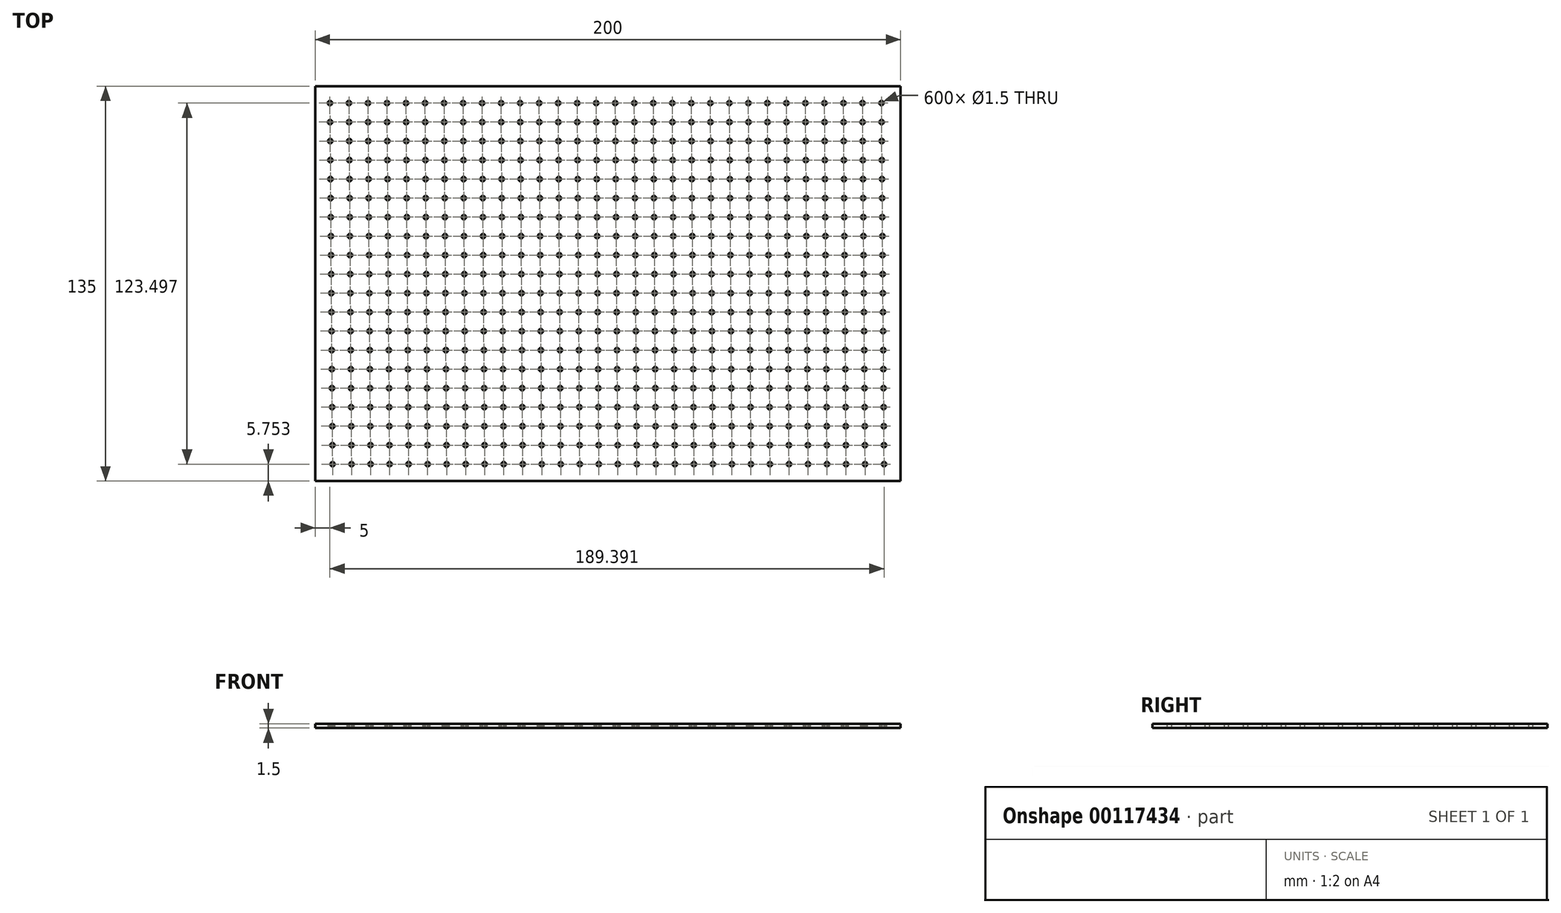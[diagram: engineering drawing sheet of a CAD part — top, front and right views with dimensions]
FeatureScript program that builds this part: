
annotation { "Feature Type Name" : "Feature", "Feature Type Description" : "" }
export const myFeature = defineFeature(function(context is Context, id is Id, definition is map)
    precondition{}
    {
        {
            var Q0;
            Q0=qCreatedBy(makeId("Top.planeOp"),FACE);
            var sketch = newSketch(context, id + "F0", { "sketchPlane" : qUnion([Q0])});
            skLineSegment(sketch, "E0.bottom", {"start": v(100, 67.5) * mm, "end": v(-100, 67.5) * mm});
            skLineSegment(sketch, "E0.top", {"start": v(100, -67.5) * mm, "end": v(-100, -67.5) * mm});
            skLineSegment(sketch, "E0.right", {"start": v(-100, 67.5) * mm, "end": v(-100, -67.5) * mm});
            skPoint(sketch, "E0.middle", {"position": v(0, 0) * mm});
            skLineSegment(sketch, "E1", {"start": v(-96.5, 67.5) * mm, "end": v(-96.5, 62.5) * mm, "construction": true});
            skLineSegment(sketch, "E2", {"start": v(-96.5, 62.5) * mm, "end": v(-100, 62.5) * mm, "construction": true});
            skLineSegment(sketch, "E3", {"start": v(-96.5, 62.5) * mm, "end": v(-95, 62.5) * mm, "construction": true});
            skLineSegment(sketch, "E4", {"start": v(-95, 62.5) * mm, "end": v(-95, 61.75) * mm, "construction": true});
            skCircle(sketch, "E5", {"center": v(-95, 61.75) * mm, "radius": 0.75 * mm});
            skCircle(sketch, "E6.1.0.0", {"center": v(-88.5, 61.75) * mm, "radius": 0.75 * mm});
            skCircle(sketch, "E6.2.0.0", {"center": v(-82, 61.75) * mm, "radius": 0.75 * mm});
            skCircle(sketch, "E6.3.0.0", {"center": v(-75.5, 61.75) * mm, "radius": 0.75 * mm});
            skCircle(sketch, "E6.4.0.0", {"center": v(-69, 61.75) * mm, "radius": 0.75 * mm});
            skCircle(sketch, "E6.5.0.0", {"center": v(-62.5, 61.75) * mm, "radius": 0.75 * mm});
            skCircle(sketch, "E6.6.0.0", {"center": v(-56, 61.75) * mm, "radius": 0.75 * mm});
            skCircle(sketch, "E6.7.0.0", {"center": v(-49.5, 61.75) * mm, "radius": 0.75 * mm});
            skCircle(sketch, "E6.8.0.0", {"center": v(-43, 61.75) * mm, "radius": 0.75 * mm});
            skCircle(sketch, "E6.9.0.0", {"center": v(-36.5, 61.75) * mm, "radius": 0.75 * mm});
            skCircle(sketch, "E6.10.0.0", {"center": v(-30, 61.75) * mm, "radius": 0.75 * mm});
            skCircle(sketch, "E6.11.0.0", {"center": v(-23.5, 61.75) * mm, "radius": 0.75 * mm});
            skCircle(sketch, "E6.12.0.0", {"center": v(-17, 61.75) * mm, "radius": 0.75 * mm});
            skCircle(sketch, "E6.13.0.0", {"center": v(-10.5, 61.75) * mm, "radius": 0.75 * mm});
            skCircle(sketch, "E6.14.0.0", {"center": v(-4, 61.75) * mm, "radius": 0.75 * mm});
            skCircle(sketch, "E6.15.0.0", {"center": v(2.5, 61.75) * mm, "radius": 0.75 * mm});
            skCircle(sketch, "E6.16.0.0", {"center": v(9, 61.75) * mm, "radius": 0.75 * mm});
            skCircle(sketch, "E6.17.0.0", {"center": v(15.5, 61.75) * mm, "radius": 0.75 * mm});
            skCircle(sketch, "E6.18.0.0", {"center": v(22, 61.75) * mm, "radius": 0.75 * mm});
            skCircle(sketch, "E6.19.0.0", {"center": v(28.5, 61.75) * mm, "radius": 0.75 * mm});
            skCircle(sketch, "E6.20.0.0", {"center": v(35, 61.75) * mm, "radius": 0.75 * mm});
            skCircle(sketch, "E6.21.0.0", {"center": v(41.5, 61.75) * mm, "radius": 0.75 * mm});
            skCircle(sketch, "E6.22.0.0", {"center": v(48, 61.75) * mm, "radius": 0.75 * mm});
            skCircle(sketch, "E6.23.0.0", {"center": v(54.5, 61.75) * mm, "radius": 0.75 * mm});
            skCircle(sketch, "E6.24.0.0", {"center": v(61, 61.75) * mm, "radius": 0.75 * mm});
            skCircle(sketch, "E6.25.0.0", {"center": v(67.5, 61.75) * mm, "radius": 0.75 * mm});
            skCircle(sketch, "E6.26.0.0", {"center": v(74, 61.75) * mm, "radius": 0.75 * mm});
            skCircle(sketch, "E6.27.0.0", {"center": v(80.5, 61.75) * mm, "radius": 0.75 * mm});
            skCircle(sketch, "E6.28.0.0", {"center": v(87, 61.75) * mm, "radius": 0.75 * mm});
            skCircle(sketch, "E6.29.0.0", {"center": v(93.5, 61.75) * mm, "radius": 0.75 * mm});
            skLineSegment(sketch, "E6.direction1", {"start": v(-95, 61.75) * mm, "end": v(-88.5, 61.75) * mm, "construction": true});
            skLineSegment(sketch, "E7", {"start": v(-95, 61.75) * mm, "end": v(-100, 61.75) * mm, "construction": true});
            skCircle(sketch, "E8.1.0.1", {"center": v(80.55, 55.25) * mm, "radius": 0.75 * mm});
            skCircle(sketch, "E8.1.0.2", {"center": v(54.55, 55.25) * mm, "radius": 0.75 * mm});
            skCircle(sketch, "E8.1.0.3", {"center": v(22.05, 55.25) * mm, "radius": 0.75 * mm});
            skCircle(sketch, "E8.1.0.7", {"center": v(28.55, 55.25) * mm, "radius": 0.75 * mm});
            skCircle(sketch, "E8.1.0.10", {"center": v(2.55, 55.25) * mm, "radius": 0.75 * mm});
            skCircle(sketch, "E8.1.0.13", {"center": v(41.55, 55.25) * mm, "radius": 0.75 * mm});
            skCircle(sketch, "E8.1.0.14", {"center": v(87.05, 55.25) * mm, "radius": 0.75 * mm});
            skCircle(sketch, "E8.1.0.16", {"center": v(61.05, 55.25) * mm, "radius": 0.75 * mm});
            skCircle(sketch, "E8.1.0.19", {"center": v(35.05, 55.25) * mm, "radius": 0.75 * mm});
            skCircle(sketch, "E8.1.0.22", {"center": v(9.05, 55.25) * mm, "radius": 0.75 * mm});
            skCircle(sketch, "E8.1.0.24", {"center": v(93.55, 55.25) * mm, "radius": 0.75 * mm});
            skCircle(sketch, "E8.1.0.25", {"center": v(48.05, 55.25) * mm, "radius": 0.75 * mm});
            skCircle(sketch, "E8.1.0.27", {"center": v(67.55, 55.25) * mm, "radius": 0.75 * mm});
            skCircle(sketch, "E8.1.0.30", {"center": v(15.55, 55.25) * mm, "radius": 0.75 * mm});
            skCircle(sketch, "E8.1.0.32", {"center": v(74.05, 55.25) * mm, "radius": 0.75 * mm});
            skCircle(sketch, "E8.1.0.35", {"center": v(-62.45, 55.25) * mm, "radius": 0.75 * mm});
            skCircle(sketch, "E8.1.0.36", {"center": v(-55.95, 55.25) * mm, "radius": 0.75 * mm});
            skCircle(sketch, "E8.1.0.37", {"center": v(-49.45, 55.25) * mm, "radius": 0.75 * mm});
            skCircle(sketch, "E8.1.0.38", {"center": v(-23.45, 55.25) * mm, "radius": 0.75 * mm});
            skCircle(sketch, "E8.1.0.39", {"center": v(-3.95, 55.25) * mm, "radius": 0.75 * mm});
            skCircle(sketch, "E8.1.0.40", {"center": v(-94.95, 55.25) * mm, "radius": 0.75 * mm});
            skCircle(sketch, "E8.1.0.41", {"center": v(-88.45, 55.25) * mm, "radius": 0.75 * mm});
            skCircle(sketch, "E8.1.0.42", {"center": v(-81.95, 55.25) * mm, "radius": 0.75 * mm});
            skCircle(sketch, "E8.1.0.43", {"center": v(-75.45, 55.25) * mm, "radius": 0.75 * mm});
            skCircle(sketch, "E8.1.0.44", {"center": v(-68.95, 55.25) * mm, "radius": 0.75 * mm});
            skCircle(sketch, "E8.1.0.45", {"center": v(-16.95, 55.25) * mm, "radius": 0.75 * mm});
            skCircle(sketch, "E8.1.0.46", {"center": v(-42.95, 55.25) * mm, "radius": 0.75 * mm});
            skCircle(sketch, "E8.1.0.47", {"center": v(-10.45, 55.25) * mm, "radius": 0.75 * mm});
            skCircle(sketch, "E8.1.0.48", {"center": v(-36.45, 55.25) * mm, "radius": 0.75 * mm});
            skCircle(sketch, "E8.1.0.49", {"center": v(-29.95, 55.25) * mm, "radius": 0.75 * mm});
            skCircle(sketch, "E8.2.0.1", {"center": v(80.6, 48.75) * mm, "radius": 0.75 * mm});
            skCircle(sketch, "E8.2.0.2", {"center": v(54.6, 48.75) * mm, "radius": 0.75 * mm});
            skCircle(sketch, "E8.2.0.3", {"center": v(22.1, 48.75) * mm, "radius": 0.75 * mm});
            skCircle(sketch, "E8.2.0.7", {"center": v(28.6, 48.75) * mm, "radius": 0.75 * mm});
            skCircle(sketch, "E8.2.0.10", {"center": v(2.6, 48.75) * mm, "radius": 0.75 * mm});
            skCircle(sketch, "E8.2.0.13", {"center": v(41.6, 48.75) * mm, "radius": 0.75 * mm});
            skCircle(sketch, "E8.2.0.14", {"center": v(87.1, 48.75) * mm, "radius": 0.75 * mm});
            skCircle(sketch, "E8.2.0.16", {"center": v(61.1, 48.75) * mm, "radius": 0.75 * mm});
            skCircle(sketch, "E8.2.0.19", {"center": v(35.1, 48.75) * mm, "radius": 0.75 * mm});
            skCircle(sketch, "E8.2.0.22", {"center": v(9.1, 48.75) * mm, "radius": 0.75 * mm});
            skCircle(sketch, "E8.2.0.24", {"center": v(93.6, 48.75) * mm, "radius": 0.75 * mm});
            skCircle(sketch, "E8.2.0.25", {"center": v(48.1, 48.75) * mm, "radius": 0.75 * mm});
            skCircle(sketch, "E8.2.0.27", {"center": v(67.6, 48.75) * mm, "radius": 0.75 * mm});
            skCircle(sketch, "E8.2.0.30", {"center": v(15.6, 48.75) * mm, "radius": 0.75 * mm});
            skCircle(sketch, "E8.2.0.32", {"center": v(74.1, 48.75) * mm, "radius": 0.75 * mm});
            skCircle(sketch, "E8.2.0.35", {"center": v(-62.4, 48.75) * mm, "radius": 0.75 * mm});
            skCircle(sketch, "E8.2.0.36", {"center": v(-55.9, 48.75) * mm, "radius": 0.75 * mm});
            skCircle(sketch, "E8.2.0.37", {"center": v(-49.4, 48.75) * mm, "radius": 0.75 * mm});
            skCircle(sketch, "E8.2.0.38", {"center": v(-23.4, 48.75) * mm, "radius": 0.75 * mm});
            skCircle(sketch, "E8.2.0.39", {"center": v(-3.9, 48.75) * mm, "radius": 0.75 * mm});
            skCircle(sketch, "E8.2.0.40", {"center": v(-94.9, 48.75) * mm, "radius": 0.75 * mm});
            skCircle(sketch, "E8.2.0.41", {"center": v(-88.4, 48.75) * mm, "radius": 0.75 * mm});
            skCircle(sketch, "E8.2.0.42", {"center": v(-81.9, 48.75) * mm, "radius": 0.75 * mm});
            skCircle(sketch, "E8.2.0.43", {"center": v(-75.4, 48.75) * mm, "radius": 0.75 * mm});
            skCircle(sketch, "E8.2.0.44", {"center": v(-68.9, 48.75) * mm, "radius": 0.75 * mm});
            skCircle(sketch, "E8.2.0.45", {"center": v(-16.9, 48.75) * mm, "radius": 0.75 * mm});
            skCircle(sketch, "E8.2.0.46", {"center": v(-42.9, 48.75) * mm, "radius": 0.75 * mm});
            skCircle(sketch, "E8.2.0.47", {"center": v(-10.4, 48.75) * mm, "radius": 0.75 * mm});
            skCircle(sketch, "E8.2.0.48", {"center": v(-36.4, 48.75) * mm, "radius": 0.75 * mm});
            skCircle(sketch, "E8.2.0.49", {"center": v(-29.9, 48.75) * mm, "radius": 0.75 * mm});
            skCircle(sketch, "E8.3.0.1", {"center": v(80.64, 42.25) * mm, "radius": 0.75 * mm});
            skCircle(sketch, "E8.3.0.2", {"center": v(54.64, 42.25) * mm, "radius": 0.75 * mm});
            skCircle(sketch, "E8.3.0.3", {"center": v(22.14, 42.25) * mm, "radius": 0.75 * mm});
            skCircle(sketch, "E8.3.0.7", {"center": v(28.64, 42.25) * mm, "radius": 0.75 * mm});
            skCircle(sketch, "E8.3.0.10", {"center": v(2.64, 42.25) * mm, "radius": 0.75 * mm});
            skCircle(sketch, "E8.3.0.13", {"center": v(41.64, 42.25) * mm, "radius": 0.75 * mm});
            skCircle(sketch, "E8.3.0.14", {"center": v(87.14, 42.25) * mm, "radius": 0.75 * mm});
            skCircle(sketch, "E8.3.0.16", {"center": v(61.14, 42.25) * mm, "radius": 0.75 * mm});
            skCircle(sketch, "E8.3.0.19", {"center": v(35.14, 42.25) * mm, "radius": 0.75 * mm});
            skCircle(sketch, "E8.3.0.22", {"center": v(9.14, 42.25) * mm, "radius": 0.75 * mm});
            skCircle(sketch, "E8.3.0.24", {"center": v(93.64, 42.25) * mm, "radius": 0.75 * mm});
            skCircle(sketch, "E8.3.0.25", {"center": v(48.14, 42.25) * mm, "radius": 0.75 * mm});
            skCircle(sketch, "E8.3.0.27", {"center": v(67.64, 42.25) * mm, "radius": 0.75 * mm});
            skCircle(sketch, "E8.3.0.30", {"center": v(15.64, 42.25) * mm, "radius": 0.75 * mm});
            skCircle(sketch, "E8.3.0.32", {"center": v(74.14, 42.25) * mm, "radius": 0.75 * mm});
            skCircle(sketch, "E8.3.0.35", {"center": v(-62.36, 42.25) * mm, "radius": 0.75 * mm});
            skCircle(sketch, "E8.3.0.36", {"center": v(-55.86, 42.25) * mm, "radius": 0.75 * mm});
            skCircle(sketch, "E8.3.0.37", {"center": v(-49.36, 42.25) * mm, "radius": 0.75 * mm});
            skCircle(sketch, "E8.3.0.38", {"center": v(-23.36, 42.25) * mm, "radius": 0.75 * mm});
            skCircle(sketch, "E8.3.0.39", {"center": v(-3.86, 42.25) * mm, "radius": 0.75 * mm});
            skCircle(sketch, "E8.3.0.40", {"center": v(-94.86, 42.25) * mm, "radius": 0.75 * mm});
            skCircle(sketch, "E8.3.0.41", {"center": v(-88.36, 42.25) * mm, "radius": 0.75 * mm});
            skCircle(sketch, "E8.3.0.42", {"center": v(-81.86, 42.25) * mm, "radius": 0.75 * mm});
            skCircle(sketch, "E8.3.0.43", {"center": v(-75.36, 42.25) * mm, "radius": 0.75 * mm});
            skCircle(sketch, "E8.3.0.44", {"center": v(-68.86, 42.25) * mm, "radius": 0.75 * mm});
            skCircle(sketch, "E8.3.0.45", {"center": v(-16.86, 42.25) * mm, "radius": 0.75 * mm});
            skCircle(sketch, "E8.3.0.46", {"center": v(-42.86, 42.25) * mm, "radius": 0.75 * mm});
            skCircle(sketch, "E8.3.0.47", {"center": v(-10.36, 42.25) * mm, "radius": 0.75 * mm});
            skCircle(sketch, "E8.3.0.48", {"center": v(-36.36, 42.25) * mm, "radius": 0.75 * mm});
            skCircle(sketch, "E8.3.0.49", {"center": v(-29.86, 42.25) * mm, "radius": 0.75 * mm});
            skCircle(sketch, "E8.4.0.1", {"center": v(80.69, 35.75) * mm, "radius": 0.75 * mm});
            skCircle(sketch, "E8.4.0.2", {"center": v(54.69, 35.75) * mm, "radius": 0.75 * mm});
            skCircle(sketch, "E8.4.0.3", {"center": v(22.19, 35.75) * mm, "radius": 0.75 * mm});
            skCircle(sketch, "E8.4.0.7", {"center": v(28.69, 35.75) * mm, "radius": 0.75 * mm});
            skCircle(sketch, "E8.4.0.10", {"center": v(2.69, 35.75) * mm, "radius": 0.75 * mm});
            skCircle(sketch, "E8.4.0.13", {"center": v(41.69, 35.75) * mm, "radius": 0.75 * mm});
            skCircle(sketch, "E8.4.0.14", {"center": v(87.19, 35.75) * mm, "radius": 0.75 * mm});
            skCircle(sketch, "E8.4.0.16", {"center": v(61.19, 35.75) * mm, "radius": 0.75 * mm});
            skCircle(sketch, "E8.4.0.19", {"center": v(35.19, 35.75) * mm, "radius": 0.75 * mm});
            skCircle(sketch, "E8.4.0.22", {"center": v(9.19, 35.75) * mm, "radius": 0.75 * mm});
            skCircle(sketch, "E8.4.0.24", {"center": v(93.69, 35.75) * mm, "radius": 0.75 * mm});
            skCircle(sketch, "E8.4.0.25", {"center": v(48.19, 35.75) * mm, "radius": 0.75 * mm});
            skCircle(sketch, "E8.4.0.27", {"center": v(67.69, 35.75) * mm, "radius": 0.75 * mm});
            skCircle(sketch, "E8.4.0.30", {"center": v(15.69, 35.75) * mm, "radius": 0.75 * mm});
            skCircle(sketch, "E8.4.0.32", {"center": v(74.19, 35.75) * mm, "radius": 0.75 * mm});
            skCircle(sketch, "E8.4.0.35", {"center": v(-62.31, 35.75) * mm, "radius": 0.75 * mm});
            skCircle(sketch, "E8.4.0.36", {"center": v(-55.81, 35.75) * mm, "radius": 0.75 * mm});
            skCircle(sketch, "E8.4.0.37", {"center": v(-49.31, 35.75) * mm, "radius": 0.75 * mm});
            skCircle(sketch, "E8.4.0.38", {"center": v(-23.31, 35.75) * mm, "radius": 0.75 * mm});
            skCircle(sketch, "E8.4.0.39", {"center": v(-3.81, 35.75) * mm, "radius": 0.75 * mm});
            skCircle(sketch, "E8.4.0.40", {"center": v(-94.81, 35.75) * mm, "radius": 0.75 * mm});
            skCircle(sketch, "E8.4.0.41", {"center": v(-88.31, 35.75) * mm, "radius": 0.75 * mm});
            skCircle(sketch, "E8.4.0.42", {"center": v(-81.81, 35.75) * mm, "radius": 0.75 * mm});
            skCircle(sketch, "E8.4.0.43", {"center": v(-75.31, 35.75) * mm, "radius": 0.75 * mm});
            skCircle(sketch, "E8.4.0.44", {"center": v(-68.81, 35.75) * mm, "radius": 0.75 * mm});
            skCircle(sketch, "E8.4.0.45", {"center": v(-16.81, 35.75) * mm, "radius": 0.75 * mm});
            skCircle(sketch, "E8.4.0.46", {"center": v(-42.81, 35.75) * mm, "radius": 0.75 * mm});
            skCircle(sketch, "E8.4.0.47", {"center": v(-10.31, 35.75) * mm, "radius": 0.75 * mm});
            skCircle(sketch, "E8.4.0.48", {"center": v(-36.31, 35.75) * mm, "radius": 0.75 * mm});
            skCircle(sketch, "E8.4.0.49", {"center": v(-29.81, 35.75) * mm, "radius": 0.75 * mm});
            skCircle(sketch, "E8.5.0.1", {"center": v(80.73, 29.25) * mm, "radius": 0.75 * mm});
            skCircle(sketch, "E8.5.0.2", {"center": v(54.73, 29.25) * mm, "radius": 0.75 * mm});
            skCircle(sketch, "E8.5.0.3", {"center": v(22.23, 29.25) * mm, "radius": 0.75 * mm});
            skCircle(sketch, "E8.5.0.7", {"center": v(28.73, 29.25) * mm, "radius": 0.75 * mm});
            skCircle(sketch, "E8.5.0.10", {"center": v(2.73, 29.25) * mm, "radius": 0.75 * mm});
            skCircle(sketch, "E8.5.0.13", {"center": v(41.73, 29.25) * mm, "radius": 0.75 * mm});
            skCircle(sketch, "E8.5.0.14", {"center": v(87.23, 29.25) * mm, "radius": 0.75 * mm});
            skCircle(sketch, "E8.5.0.16", {"center": v(61.23, 29.25) * mm, "radius": 0.75 * mm});
            skCircle(sketch, "E8.5.0.19", {"center": v(35.23, 29.25) * mm, "radius": 0.75 * mm});
            skCircle(sketch, "E8.5.0.22", {"center": v(9.23, 29.25) * mm, "radius": 0.75 * mm});
            skCircle(sketch, "E8.5.0.24", {"center": v(93.73, 29.25) * mm, "radius": 0.75 * mm});
            skCircle(sketch, "E8.5.0.25", {"center": v(48.23, 29.25) * mm, "radius": 0.75 * mm});
            skCircle(sketch, "E8.5.0.27", {"center": v(67.73, 29.25) * mm, "radius": 0.75 * mm});
            skCircle(sketch, "E8.5.0.30", {"center": v(15.73, 29.25) * mm, "radius": 0.75 * mm});
            skCircle(sketch, "E8.5.0.32", {"center": v(74.23, 29.25) * mm, "radius": 0.75 * mm});
            skCircle(sketch, "E8.5.0.35", {"center": v(-62.27, 29.25) * mm, "radius": 0.75 * mm});
            skCircle(sketch, "E8.5.0.36", {"center": v(-55.77, 29.25) * mm, "radius": 0.75 * mm});
            skCircle(sketch, "E8.5.0.37", {"center": v(-49.27, 29.25) * mm, "radius": 0.75 * mm});
            skCircle(sketch, "E8.5.0.38", {"center": v(-23.27, 29.25) * mm, "radius": 0.75 * mm});
            skCircle(sketch, "E8.5.0.39", {"center": v(-3.77, 29.25) * mm, "radius": 0.75 * mm});
            skCircle(sketch, "E8.5.0.40", {"center": v(-94.77, 29.25) * mm, "radius": 0.75 * mm});
            skCircle(sketch, "E8.5.0.41", {"center": v(-88.27, 29.25) * mm, "radius": 0.75 * mm});
            skCircle(sketch, "E8.5.0.42", {"center": v(-81.77, 29.25) * mm, "radius": 0.75 * mm});
            skCircle(sketch, "E8.5.0.43", {"center": v(-75.27, 29.25) * mm, "radius": 0.75 * mm});
            skCircle(sketch, "E8.5.0.44", {"center": v(-68.77, 29.25) * mm, "radius": 0.75 * mm});
            skCircle(sketch, "E8.5.0.45", {"center": v(-16.77, 29.25) * mm, "radius": 0.75 * mm});
            skCircle(sketch, "E8.5.0.46", {"center": v(-42.77, 29.25) * mm, "radius": 0.75 * mm});
            skCircle(sketch, "E8.5.0.47", {"center": v(-10.27, 29.25) * mm, "radius": 0.75 * mm});
            skCircle(sketch, "E8.5.0.48", {"center": v(-36.27, 29.25) * mm, "radius": 0.75 * mm});
            skCircle(sketch, "E8.5.0.49", {"center": v(-29.77, 29.25) * mm, "radius": 0.75 * mm});
            skCircle(sketch, "E8.6.0.1", {"center": v(80.78, 22.75) * mm, "radius": 0.75 * mm});
            skCircle(sketch, "E8.6.0.2", {"center": v(54.78, 22.75) * mm, "radius": 0.75 * mm});
            skCircle(sketch, "E8.6.0.3", {"center": v(22.28, 22.75) * mm, "radius": 0.75 * mm});
            skCircle(sketch, "E8.6.0.7", {"center": v(28.78, 22.75) * mm, "radius": 0.75 * mm});
            skCircle(sketch, "E8.6.0.10", {"center": v(2.78, 22.75) * mm, "radius": 0.75 * mm});
            skCircle(sketch, "E8.6.0.13", {"center": v(41.78, 22.75) * mm, "radius": 0.75 * mm});
            skCircle(sketch, "E8.6.0.14", {"center": v(87.28, 22.75) * mm, "radius": 0.75 * mm});
            skCircle(sketch, "E8.6.0.16", {"center": v(61.28, 22.75) * mm, "radius": 0.75 * mm});
            skCircle(sketch, "E8.6.0.19", {"center": v(35.28, 22.75) * mm, "radius": 0.75 * mm});
            skCircle(sketch, "E8.6.0.22", {"center": v(9.28, 22.75) * mm, "radius": 0.75 * mm});
            skCircle(sketch, "E8.6.0.24", {"center": v(93.78, 22.75) * mm, "radius": 0.75 * mm});
            skCircle(sketch, "E8.6.0.25", {"center": v(48.28, 22.75) * mm, "radius": 0.75 * mm});
            skCircle(sketch, "E8.6.0.27", {"center": v(67.78, 22.75) * mm, "radius": 0.75 * mm});
            skCircle(sketch, "E8.6.0.30", {"center": v(15.78, 22.75) * mm, "radius": 0.75 * mm});
            skCircle(sketch, "E8.6.0.32", {"center": v(74.28, 22.75) * mm, "radius": 0.75 * mm});
            skCircle(sketch, "E8.6.0.35", {"center": v(-62.22, 22.75) * mm, "radius": 0.75 * mm});
            skCircle(sketch, "E8.6.0.36", {"center": v(-55.72, 22.75) * mm, "radius": 0.75 * mm});
            skCircle(sketch, "E8.6.0.37", {"center": v(-49.22, 22.75) * mm, "radius": 0.75 * mm});
            skCircle(sketch, "E8.6.0.38", {"center": v(-23.22, 22.75) * mm, "radius": 0.75 * mm});
            skCircle(sketch, "E8.6.0.39", {"center": v(-3.72, 22.75) * mm, "radius": 0.75 * mm});
            skCircle(sketch, "E8.6.0.40", {"center": v(-94.72, 22.75) * mm, "radius": 0.75 * mm});
            skCircle(sketch, "E8.6.0.41", {"center": v(-88.22, 22.75) * mm, "radius": 0.75 * mm});
            skCircle(sketch, "E8.6.0.42", {"center": v(-81.72, 22.75) * mm, "radius": 0.75 * mm});
            skCircle(sketch, "E8.6.0.43", {"center": v(-75.22, 22.75) * mm, "radius": 0.75 * mm});
            skCircle(sketch, "E8.6.0.44", {"center": v(-68.72, 22.75) * mm, "radius": 0.75 * mm});
            skCircle(sketch, "E8.6.0.45", {"center": v(-16.72, 22.75) * mm, "radius": 0.75 * mm});
            skCircle(sketch, "E8.6.0.46", {"center": v(-42.72, 22.75) * mm, "radius": 0.75 * mm});
            skCircle(sketch, "E8.6.0.47", {"center": v(-10.22, 22.75) * mm, "radius": 0.75 * mm});
            skCircle(sketch, "E8.6.0.48", {"center": v(-36.22, 22.75) * mm, "radius": 0.75 * mm});
            skCircle(sketch, "E8.6.0.49", {"center": v(-29.72, 22.75) * mm, "radius": 0.75 * mm});
            skCircle(sketch, "E8.7.0.1", {"center": v(80.83, 16.25) * mm, "radius": 0.75 * mm});
            skCircle(sketch, "E8.7.0.2", {"center": v(54.83, 16.25) * mm, "radius": 0.75 * mm});
            skCircle(sketch, "E8.7.0.3", {"center": v(22.33, 16.25) * mm, "radius": 0.75 * mm});
            skCircle(sketch, "E8.7.0.7", {"center": v(28.83, 16.25) * mm, "radius": 0.75 * mm});
            skCircle(sketch, "E8.7.0.10", {"center": v(2.83, 16.25) * mm, "radius": 0.75 * mm});
            skCircle(sketch, "E8.7.0.13", {"center": v(41.83, 16.25) * mm, "radius": 0.75 * mm});
            skCircle(sketch, "E8.7.0.14", {"center": v(87.33, 16.25) * mm, "radius": 0.75 * mm});
            skCircle(sketch, "E8.7.0.16", {"center": v(61.33, 16.25) * mm, "radius": 0.75 * mm});
            skCircle(sketch, "E8.7.0.19", {"center": v(35.33, 16.25) * mm, "radius": 0.75 * mm});
            skCircle(sketch, "E8.7.0.22", {"center": v(9.33, 16.25) * mm, "radius": 0.75 * mm});
            skCircle(sketch, "E8.7.0.24", {"center": v(93.83, 16.25) * mm, "radius": 0.75 * mm});
            skCircle(sketch, "E8.7.0.25", {"center": v(48.33, 16.25) * mm, "radius": 0.75 * mm});
            skCircle(sketch, "E8.7.0.27", {"center": v(67.83, 16.25) * mm, "radius": 0.75 * mm});
            skCircle(sketch, "E8.7.0.30", {"center": v(15.83, 16.25) * mm, "radius": 0.75 * mm});
            skCircle(sketch, "E8.7.0.32", {"center": v(74.33, 16.25) * mm, "radius": 0.75 * mm});
            skCircle(sketch, "E8.7.0.35", {"center": v(-62.17, 16.25) * mm, "radius": 0.75 * mm});
            skCircle(sketch, "E8.7.0.36", {"center": v(-55.67, 16.25) * mm, "radius": 0.75 * mm});
            skCircle(sketch, "E8.7.0.37", {"center": v(-49.17, 16.25) * mm, "radius": 0.75 * mm});
            skCircle(sketch, "E8.7.0.38", {"center": v(-23.17, 16.25) * mm, "radius": 0.75 * mm});
            skCircle(sketch, "E8.7.0.39", {"center": v(-3.67, 16.25) * mm, "radius": 0.75 * mm});
            skCircle(sketch, "E8.7.0.40", {"center": v(-94.67, 16.25) * mm, "radius": 0.75 * mm});
            skCircle(sketch, "E8.7.0.41", {"center": v(-88.17, 16.25) * mm, "radius": 0.75 * mm});
            skCircle(sketch, "E8.7.0.42", {"center": v(-81.67, 16.25) * mm, "radius": 0.75 * mm});
            skCircle(sketch, "E8.7.0.43", {"center": v(-75.17, 16.25) * mm, "radius": 0.75 * mm});
            skCircle(sketch, "E8.7.0.44", {"center": v(-68.67, 16.25) * mm, "radius": 0.75 * mm});
            skCircle(sketch, "E8.7.0.45", {"center": v(-16.67, 16.25) * mm, "radius": 0.75 * mm});
            skCircle(sketch, "E8.7.0.46", {"center": v(-42.67, 16.25) * mm, "radius": 0.75 * mm});
            skCircle(sketch, "E8.7.0.47", {"center": v(-10.17, 16.25) * mm, "radius": 0.75 * mm});
            skCircle(sketch, "E8.7.0.48", {"center": v(-36.17, 16.25) * mm, "radius": 0.75 * mm});
            skCircle(sketch, "E8.7.0.49", {"center": v(-29.67, 16.25) * mm, "radius": 0.75 * mm});
            skCircle(sketch, "E8.8.0.1", {"center": v(80.88, 9.75) * mm, "radius": 0.75 * mm});
            skCircle(sketch, "E8.8.0.2", {"center": v(54.88, 9.75) * mm, "radius": 0.75 * mm});
            skCircle(sketch, "E8.8.0.3", {"center": v(22.38, 9.75) * mm, "radius": 0.75 * mm});
            skCircle(sketch, "E8.8.0.7", {"center": v(28.88, 9.75) * mm, "radius": 0.75 * mm});
            skCircle(sketch, "E8.8.0.10", {"center": v(2.88, 9.75) * mm, "radius": 0.75 * mm});
            skCircle(sketch, "E8.8.0.13", {"center": v(41.88, 9.75) * mm, "radius": 0.75 * mm});
            skCircle(sketch, "E8.8.0.14", {"center": v(87.38, 9.75) * mm, "radius": 0.75 * mm});
            skCircle(sketch, "E8.8.0.16", {"center": v(61.38, 9.75) * mm, "radius": 0.75 * mm});
            skCircle(sketch, "E8.8.0.19", {"center": v(35.38, 9.75) * mm, "radius": 0.75 * mm});
            skCircle(sketch, "E8.8.0.22", {"center": v(9.38, 9.75) * mm, "radius": 0.75 * mm});
            skCircle(sketch, "E8.8.0.24", {"center": v(93.88, 9.75) * mm, "radius": 0.75 * mm});
            skCircle(sketch, "E8.8.0.25", {"center": v(48.38, 9.75) * mm, "radius": 0.75 * mm});
            skCircle(sketch, "E8.8.0.27", {"center": v(67.88, 9.75) * mm, "radius": 0.75 * mm});
            skCircle(sketch, "E8.8.0.30", {"center": v(15.88, 9.75) * mm, "radius": 0.75 * mm});
            skCircle(sketch, "E8.8.0.32", {"center": v(74.38, 9.75) * mm, "radius": 0.75 * mm});
            skCircle(sketch, "E8.8.0.35", {"center": v(-62.12, 9.75) * mm, "radius": 0.75 * mm});
            skCircle(sketch, "E8.8.0.36", {"center": v(-55.62, 9.75) * mm, "radius": 0.75 * mm});
            skCircle(sketch, "E8.8.0.37", {"center": v(-49.12, 9.75) * mm, "radius": 0.75 * mm});
            skCircle(sketch, "E8.8.0.38", {"center": v(-23.12, 9.75) * mm, "radius": 0.75 * mm});
            skCircle(sketch, "E8.8.0.39", {"center": v(-3.62, 9.75) * mm, "radius": 0.75 * mm});
            skCircle(sketch, "E8.8.0.40", {"center": v(-94.62, 9.75) * mm, "radius": 0.75 * mm});
            skCircle(sketch, "E8.8.0.41", {"center": v(-88.12, 9.75) * mm, "radius": 0.75 * mm});
            skCircle(sketch, "E8.8.0.42", {"center": v(-81.62, 9.75) * mm, "radius": 0.75 * mm});
            skCircle(sketch, "E8.8.0.43", {"center": v(-75.12, 9.75) * mm, "radius": 0.75 * mm});
            skCircle(sketch, "E8.8.0.44", {"center": v(-68.62, 9.75) * mm, "radius": 0.75 * mm});
            skCircle(sketch, "E8.8.0.45", {"center": v(-16.62, 9.75) * mm, "radius": 0.75 * mm});
            skCircle(sketch, "E8.8.0.46", {"center": v(-42.62, 9.75) * mm, "radius": 0.75 * mm});
            skCircle(sketch, "E8.8.0.47", {"center": v(-10.12, 9.75) * mm, "radius": 0.75 * mm});
            skCircle(sketch, "E8.8.0.48", {"center": v(-36.12, 9.75) * mm, "radius": 0.75 * mm});
            skCircle(sketch, "E8.8.0.49", {"center": v(-29.62, 9.75) * mm, "radius": 0.75 * mm});
            skCircle(sketch, "E8.9.0.1", {"center": v(80.92, 3.25) * mm, "radius": 0.75 * mm});
            skCircle(sketch, "E8.9.0.2", {"center": v(54.92, 3.25) * mm, "radius": 0.75 * mm});
            skCircle(sketch, "E8.9.0.3", {"center": v(22.42, 3.25) * mm, "radius": 0.75 * mm});
            skCircle(sketch, "E8.9.0.7", {"center": v(28.92, 3.25) * mm, "radius": 0.75 * mm});
            skCircle(sketch, "E8.9.0.10", {"center": v(2.92, 3.25) * mm, "radius": 0.75 * mm});
            skCircle(sketch, "E8.9.0.13", {"center": v(41.92, 3.25) * mm, "radius": 0.75 * mm});
            skCircle(sketch, "E8.9.0.14", {"center": v(87.42, 3.25) * mm, "radius": 0.75 * mm});
            skCircle(sketch, "E8.9.0.16", {"center": v(61.42, 3.25) * mm, "radius": 0.75 * mm});
            skCircle(sketch, "E8.9.0.19", {"center": v(35.42, 3.25) * mm, "radius": 0.75 * mm});
            skCircle(sketch, "E8.9.0.22", {"center": v(9.42, 3.25) * mm, "radius": 0.75 * mm});
            skCircle(sketch, "E8.9.0.24", {"center": v(93.92, 3.25) * mm, "radius": 0.75 * mm});
            skCircle(sketch, "E8.9.0.25", {"center": v(48.42, 3.25) * mm, "radius": 0.75 * mm});
            skCircle(sketch, "E8.9.0.27", {"center": v(67.92, 3.25) * mm, "radius": 0.75 * mm});
            skCircle(sketch, "E8.9.0.30", {"center": v(15.92, 3.25) * mm, "radius": 0.75 * mm});
            skCircle(sketch, "E8.9.0.32", {"center": v(74.42, 3.25) * mm, "radius": 0.75 * mm});
            skCircle(sketch, "E8.9.0.35", {"center": v(-62.08, 3.25) * mm, "radius": 0.75 * mm});
            skCircle(sketch, "E8.9.0.36", {"center": v(-55.58, 3.25) * mm, "radius": 0.75 * mm});
            skCircle(sketch, "E8.9.0.37", {"center": v(-49.08, 3.25) * mm, "radius": 0.75 * mm});
            skCircle(sketch, "E8.9.0.38", {"center": v(-23.08, 3.25) * mm, "radius": 0.75 * mm});
            skCircle(sketch, "E8.9.0.39", {"center": v(-3.58, 3.25) * mm, "radius": 0.75 * mm});
            skCircle(sketch, "E8.9.0.40", {"center": v(-94.58, 3.25) * mm, "radius": 0.75 * mm});
            skCircle(sketch, "E8.9.0.41", {"center": v(-88.08, 3.25) * mm, "radius": 0.75 * mm});
            skCircle(sketch, "E8.9.0.42", {"center": v(-81.58, 3.25) * mm, "radius": 0.75 * mm});
            skCircle(sketch, "E8.9.0.43", {"center": v(-75.08, 3.25) * mm, "radius": 0.75 * mm});
            skCircle(sketch, "E8.9.0.44", {"center": v(-68.58, 3.25) * mm, "radius": 0.75 * mm});
            skCircle(sketch, "E8.9.0.45", {"center": v(-16.58, 3.25) * mm, "radius": 0.75 * mm});
            skCircle(sketch, "E8.9.0.46", {"center": v(-42.58, 3.25) * mm, "radius": 0.75 * mm});
            skCircle(sketch, "E8.9.0.47", {"center": v(-10.08, 3.25) * mm, "radius": 0.75 * mm});
            skCircle(sketch, "E8.9.0.48", {"center": v(-36.08, 3.25) * mm, "radius": 0.75 * mm});
            skCircle(sketch, "E8.9.0.49", {"center": v(-29.58, 3.25) * mm, "radius": 0.75 * mm});
            skCircle(sketch, "E8.10.0.1", {"center": v(80.97, -3.25) * mm, "radius": 0.75 * mm});
            skCircle(sketch, "E8.10.0.2", {"center": v(54.97, -3.25) * mm, "radius": 0.75 * mm});
            skCircle(sketch, "E8.10.0.3", {"center": v(22.47, -3.25) * mm, "radius": 0.75 * mm});
            skCircle(sketch, "E8.10.0.7", {"center": v(28.97, -3.25) * mm, "radius": 0.75 * mm});
            skCircle(sketch, "E8.10.0.10", {"center": v(2.97, -3.25) * mm, "radius": 0.75 * mm});
            skCircle(sketch, "E8.10.0.13", {"center": v(41.97, -3.25) * mm, "radius": 0.75 * mm});
            skCircle(sketch, "E8.10.0.14", {"center": v(87.47, -3.25) * mm, "radius": 0.75 * mm});
            skCircle(sketch, "E8.10.0.16", {"center": v(61.47, -3.25) * mm, "radius": 0.75 * mm});
            skCircle(sketch, "E8.10.0.19", {"center": v(35.47, -3.25) * mm, "radius": 0.75 * mm});
            skCircle(sketch, "E8.10.0.22", {"center": v(9.47, -3.25) * mm, "radius": 0.75 * mm});
            skCircle(sketch, "E8.10.0.24", {"center": v(93.97, -3.25) * mm, "radius": 0.75 * mm});
            skCircle(sketch, "E8.10.0.25", {"center": v(48.47, -3.25) * mm, "radius": 0.75 * mm});
            skCircle(sketch, "E8.10.0.27", {"center": v(67.97, -3.25) * mm, "radius": 0.75 * mm});
            skCircle(sketch, "E8.10.0.30", {"center": v(15.97, -3.25) * mm, "radius": 0.75 * mm});
            skCircle(sketch, "E8.10.0.32", {"center": v(74.47, -3.25) * mm, "radius": 0.75 * mm});
            skCircle(sketch, "E8.10.0.35", {"center": v(-62.03, -3.25) * mm, "radius": 0.75 * mm});
            skCircle(sketch, "E8.10.0.36", {"center": v(-55.53, -3.25) * mm, "radius": 0.75 * mm});
            skCircle(sketch, "E8.10.0.37", {"center": v(-49.03, -3.25) * mm, "radius": 0.75 * mm});
            skCircle(sketch, "E8.10.0.38", {"center": v(-23.03, -3.25) * mm, "radius": 0.75 * mm});
            skCircle(sketch, "E8.10.0.39", {"center": v(-3.53, -3.25) * mm, "radius": 0.75 * mm});
            skCircle(sketch, "E8.10.0.40", {"center": v(-94.53, -3.25) * mm, "radius": 0.75 * mm});
            skCircle(sketch, "E8.10.0.41", {"center": v(-88.03, -3.25) * mm, "radius": 0.75 * mm});
            skCircle(sketch, "E8.10.0.42", {"center": v(-81.53, -3.25) * mm, "radius": 0.75 * mm});
            skCircle(sketch, "E8.10.0.43", {"center": v(-75.03, -3.25) * mm, "radius": 0.75 * mm});
            skCircle(sketch, "E8.10.0.44", {"center": v(-68.53, -3.25) * mm, "radius": 0.75 * mm});
            skCircle(sketch, "E8.10.0.45", {"center": v(-16.53, -3.25) * mm, "radius": 0.75 * mm});
            skCircle(sketch, "E8.10.0.46", {"center": v(-42.53, -3.25) * mm, "radius": 0.75 * mm});
            skCircle(sketch, "E8.10.0.47", {"center": v(-10.03, -3.25) * mm, "radius": 0.75 * mm});
            skCircle(sketch, "E8.10.0.48", {"center": v(-36.03, -3.25) * mm, "radius": 0.75 * mm});
            skCircle(sketch, "E8.10.0.49", {"center": v(-29.53, -3.25) * mm, "radius": 0.75 * mm});
            skCircle(sketch, "E8.11.0.1", {"center": v(81.02, -9.75) * mm, "radius": 0.75 * mm});
            skCircle(sketch, "E8.11.0.2", {"center": v(55.02, -9.75) * mm, "radius": 0.75 * mm});
            skCircle(sketch, "E8.11.0.3", {"center": v(22.52, -9.75) * mm, "radius": 0.75 * mm});
            skCircle(sketch, "E8.11.0.7", {"center": v(29.02, -9.75) * mm, "radius": 0.75 * mm});
            skCircle(sketch, "E8.11.0.10", {"center": v(3.02, -9.75) * mm, "radius": 0.75 * mm});
            skCircle(sketch, "E8.11.0.13", {"center": v(42.02, -9.75) * mm, "radius": 0.75 * mm});
            skCircle(sketch, "E8.11.0.14", {"center": v(87.52, -9.75) * mm, "radius": 0.75 * mm});
            skCircle(sketch, "E8.11.0.16", {"center": v(61.52, -9.75) * mm, "radius": 0.75 * mm});
            skCircle(sketch, "E8.11.0.19", {"center": v(35.52, -9.75) * mm, "radius": 0.75 * mm});
            skCircle(sketch, "E8.11.0.22", {"center": v(9.52, -9.75) * mm, "radius": 0.75 * mm});
            skCircle(sketch, "E8.11.0.24", {"center": v(94.02, -9.75) * mm, "radius": 0.75 * mm});
            skCircle(sketch, "E8.11.0.25", {"center": v(48.52, -9.75) * mm, "radius": 0.75 * mm});
            skCircle(sketch, "E8.11.0.27", {"center": v(68.02, -9.75) * mm, "radius": 0.75 * mm});
            skCircle(sketch, "E8.11.0.30", {"center": v(16.02, -9.75) * mm, "radius": 0.75 * mm});
            skCircle(sketch, "E8.11.0.32", {"center": v(74.52, -9.75) * mm, "radius": 0.75 * mm});
            skCircle(sketch, "E8.11.0.35", {"center": v(-61.98, -9.75) * mm, "radius": 0.75 * mm});
            skCircle(sketch, "E8.11.0.36", {"center": v(-55.48, -9.75) * mm, "radius": 0.75 * mm});
            skCircle(sketch, "E8.11.0.37", {"center": v(-48.98, -9.75) * mm, "radius": 0.75 * mm});
            skCircle(sketch, "E8.11.0.38", {"center": v(-22.98, -9.75) * mm, "radius": 0.75 * mm});
            skCircle(sketch, "E8.11.0.39", {"center": v(-3.48, -9.75) * mm, "radius": 0.75 * mm});
            skCircle(sketch, "E8.11.0.40", {"center": v(-94.48, -9.75) * mm, "radius": 0.75 * mm});
            skCircle(sketch, "E8.11.0.41", {"center": v(-87.98, -9.75) * mm, "radius": 0.75 * mm});
            skCircle(sketch, "E8.11.0.42", {"center": v(-81.48, -9.75) * mm, "radius": 0.75 * mm});
            skCircle(sketch, "E8.11.0.43", {"center": v(-74.98, -9.75) * mm, "radius": 0.75 * mm});
            skCircle(sketch, "E8.11.0.44", {"center": v(-68.48, -9.75) * mm, "radius": 0.75 * mm});
            skCircle(sketch, "E8.11.0.45", {"center": v(-16.48, -9.75) * mm, "radius": 0.75 * mm});
            skCircle(sketch, "E8.11.0.46", {"center": v(-42.48, -9.75) * mm, "radius": 0.75 * mm});
            skCircle(sketch, "E8.11.0.47", {"center": v(-9.98, -9.75) * mm, "radius": 0.75 * mm});
            skCircle(sketch, "E8.11.0.48", {"center": v(-35.98, -9.75) * mm, "radius": 0.75 * mm});
            skCircle(sketch, "E8.11.0.49", {"center": v(-29.48, -9.75) * mm, "radius": 0.75 * mm});
            skCircle(sketch, "E8.12.0.1", {"center": v(81.06, -16.25) * mm, "radius": 0.75 * mm});
            skCircle(sketch, "E8.12.0.2", {"center": v(55.06, -16.25) * mm, "radius": 0.75 * mm});
            skCircle(sketch, "E8.12.0.3", {"center": v(22.56, -16.25) * mm, "radius": 0.75 * mm});
            skCircle(sketch, "E8.12.0.7", {"center": v(29.06, -16.25) * mm, "radius": 0.75 * mm});
            skCircle(sketch, "E8.12.0.10", {"center": v(3.06, -16.25) * mm, "radius": 0.75 * mm});
            skCircle(sketch, "E8.12.0.13", {"center": v(42.06, -16.25) * mm, "radius": 0.75 * mm});
            skCircle(sketch, "E8.12.0.14", {"center": v(87.56, -16.25) * mm, "radius": 0.75 * mm});
            skCircle(sketch, "E8.12.0.16", {"center": v(61.56, -16.25) * mm, "radius": 0.75 * mm});
            skCircle(sketch, "E8.12.0.19", {"center": v(35.56, -16.25) * mm, "radius": 0.75 * mm});
            skCircle(sketch, "E8.12.0.22", {"center": v(9.56, -16.25) * mm, "radius": 0.75 * mm});
            skCircle(sketch, "E8.12.0.24", {"center": v(94.06, -16.25) * mm, "radius": 0.75 * mm});
            skCircle(sketch, "E8.12.0.25", {"center": v(48.56, -16.25) * mm, "radius": 0.75 * mm});
            skCircle(sketch, "E8.12.0.27", {"center": v(68.06, -16.25) * mm, "radius": 0.75 * mm});
            skCircle(sketch, "E8.12.0.30", {"center": v(16.06, -16.25) * mm, "radius": 0.75 * mm});
            skCircle(sketch, "E8.12.0.32", {"center": v(74.56, -16.25) * mm, "radius": 0.75 * mm});
            skCircle(sketch, "E8.12.0.35", {"center": v(-61.94, -16.25) * mm, "radius": 0.75 * mm});
            skCircle(sketch, "E8.12.0.36", {"center": v(-55.44, -16.25) * mm, "radius": 0.75 * mm});
            skCircle(sketch, "E8.12.0.37", {"center": v(-48.94, -16.25) * mm, "radius": 0.75 * mm});
            skCircle(sketch, "E8.12.0.38", {"center": v(-22.94, -16.25) * mm, "radius": 0.75 * mm});
            skCircle(sketch, "E8.12.0.39", {"center": v(-3.44, -16.25) * mm, "radius": 0.75 * mm});
            skCircle(sketch, "E8.12.0.40", {"center": v(-94.44, -16.25) * mm, "radius": 0.75 * mm});
            skCircle(sketch, "E8.12.0.41", {"center": v(-87.94, -16.25) * mm, "radius": 0.75 * mm});
            skCircle(sketch, "E8.12.0.42", {"center": v(-81.44, -16.25) * mm, "radius": 0.75 * mm});
            skCircle(sketch, "E8.12.0.43", {"center": v(-74.94, -16.25) * mm, "radius": 0.75 * mm});
            skCircle(sketch, "E8.12.0.44", {"center": v(-68.44, -16.25) * mm, "radius": 0.75 * mm});
            skCircle(sketch, "E8.12.0.45", {"center": v(-16.44, -16.25) * mm, "radius": 0.75 * mm});
            skCircle(sketch, "E8.12.0.46", {"center": v(-42.44, -16.25) * mm, "radius": 0.75 * mm});
            skCircle(sketch, "E8.12.0.47", {"center": v(-9.94, -16.25) * mm, "radius": 0.75 * mm});
            skCircle(sketch, "E8.12.0.48", {"center": v(-35.94, -16.25) * mm, "radius": 0.75 * mm});
            skCircle(sketch, "E8.12.0.49", {"center": v(-29.44, -16.25) * mm, "radius": 0.75 * mm});
            skCircle(sketch, "E8.13.0.1", {"center": v(81.1, -22.75) * mm, "radius": 0.75 * mm});
            skCircle(sketch, "E8.13.0.2", {"center": v(55.1, -22.75) * mm, "radius": 0.75 * mm});
            skCircle(sketch, "E8.13.0.3", {"center": v(22.6, -22.75) * mm, "radius": 0.75 * mm});
            skCircle(sketch, "E8.13.0.7", {"center": v(29.1, -22.75) * mm, "radius": 0.75 * mm});
            skCircle(sketch, "E8.13.0.10", {"center": v(3.1, -22.75) * mm, "radius": 0.75 * mm});
            skCircle(sketch, "E8.13.0.13", {"center": v(42.1, -22.75) * mm, "radius": 0.75 * mm});
            skCircle(sketch, "E8.13.0.14", {"center": v(87.6, -22.75) * mm, "radius": 0.75 * mm});
            skCircle(sketch, "E8.13.0.16", {"center": v(61.6, -22.75) * mm, "radius": 0.75 * mm});
            skCircle(sketch, "E8.13.0.19", {"center": v(35.6, -22.75) * mm, "radius": 0.75 * mm});
            skCircle(sketch, "E8.13.0.22", {"center": v(9.6, -22.75) * mm, "radius": 0.75 * mm});
            skCircle(sketch, "E8.13.0.24", {"center": v(94.1, -22.75) * mm, "radius": 0.75 * mm});
            skCircle(sketch, "E8.13.0.25", {"center": v(48.6, -22.75) * mm, "radius": 0.75 * mm});
            skCircle(sketch, "E8.13.0.27", {"center": v(68.1, -22.75) * mm, "radius": 0.75 * mm});
            skCircle(sketch, "E8.13.0.30", {"center": v(16.1, -22.75) * mm, "radius": 0.75 * mm});
            skCircle(sketch, "E8.13.0.32", {"center": v(74.6, -22.75) * mm, "radius": 0.75 * mm});
            skCircle(sketch, "E8.13.0.35", {"center": v(-61.9, -22.75) * mm, "radius": 0.75 * mm});
            skCircle(sketch, "E8.13.0.36", {"center": v(-55.4, -22.75) * mm, "radius": 0.75 * mm});
            skCircle(sketch, "E8.13.0.37", {"center": v(-48.9, -22.75) * mm, "radius": 0.75 * mm});
            skCircle(sketch, "E8.13.0.38", {"center": v(-22.9, -22.75) * mm, "radius": 0.75 * mm});
            skCircle(sketch, "E8.13.0.39", {"center": v(-3.4, -22.75) * mm, "radius": 0.75 * mm});
            skCircle(sketch, "E8.13.0.40", {"center": v(-94.4, -22.75) * mm, "radius": 0.75 * mm});
            skCircle(sketch, "E8.13.0.41", {"center": v(-87.9, -22.75) * mm, "radius": 0.75 * mm});
            skCircle(sketch, "E8.13.0.42", {"center": v(-81.4, -22.75) * mm, "radius": 0.75 * mm});
            skCircle(sketch, "E8.13.0.43", {"center": v(-74.9, -22.75) * mm, "radius": 0.75 * mm});
            skCircle(sketch, "E8.13.0.44", {"center": v(-68.4, -22.75) * mm, "radius": 0.75 * mm});
            skCircle(sketch, "E8.13.0.45", {"center": v(-16.4, -22.75) * mm, "radius": 0.75 * mm});
            skCircle(sketch, "E8.13.0.46", {"center": v(-42.4, -22.75) * mm, "radius": 0.75 * mm});
            skCircle(sketch, "E8.13.0.47", {"center": v(-9.9, -22.75) * mm, "radius": 0.75 * mm});
            skCircle(sketch, "E8.13.0.48", {"center": v(-35.9, -22.75) * mm, "radius": 0.75 * mm});
            skCircle(sketch, "E8.13.0.49", {"center": v(-29.4, -22.75) * mm, "radius": 0.75 * mm});
            skCircle(sketch, "E8.14.0.1", {"center": v(81.16, -29.25) * mm, "radius": 0.75 * mm});
            skCircle(sketch, "E8.14.0.2", {"center": v(55.16, -29.25) * mm, "radius": 0.75 * mm});
            skCircle(sketch, "E8.14.0.3", {"center": v(22.66, -29.25) * mm, "radius": 0.75 * mm});
            skCircle(sketch, "E8.14.0.7", {"center": v(29.16, -29.25) * mm, "radius": 0.75 * mm});
            skCircle(sketch, "E8.14.0.10", {"center": v(3.16, -29.25) * mm, "radius": 0.75 * mm});
            skCircle(sketch, "E8.14.0.13", {"center": v(42.16, -29.25) * mm, "radius": 0.75 * mm});
            skCircle(sketch, "E8.14.0.14", {"center": v(87.66, -29.25) * mm, "radius": 0.75 * mm});
            skCircle(sketch, "E8.14.0.16", {"center": v(61.66, -29.25) * mm, "radius": 0.75 * mm});
            skCircle(sketch, "E8.14.0.19", {"center": v(35.66, -29.25) * mm, "radius": 0.75 * mm});
            skCircle(sketch, "E8.14.0.22", {"center": v(9.66, -29.25) * mm, "radius": 0.75 * mm});
            skCircle(sketch, "E8.14.0.24", {"center": v(94.16, -29.25) * mm, "radius": 0.75 * mm});
            skCircle(sketch, "E8.14.0.25", {"center": v(48.66, -29.25) * mm, "radius": 0.75 * mm});
            skCircle(sketch, "E8.14.0.27", {"center": v(68.16, -29.25) * mm, "radius": 0.75 * mm});
            skCircle(sketch, "E8.14.0.30", {"center": v(16.16, -29.25) * mm, "radius": 0.75 * mm});
            skCircle(sketch, "E8.14.0.32", {"center": v(74.66, -29.25) * mm, "radius": 0.75 * mm});
            skCircle(sketch, "E8.14.0.35", {"center": v(-61.84, -29.25) * mm, "radius": 0.75 * mm});
            skCircle(sketch, "E8.14.0.36", {"center": v(-55.34, -29.25) * mm, "radius": 0.75 * mm});
            skCircle(sketch, "E8.14.0.37", {"center": v(-48.84, -29.25) * mm, "radius": 0.75 * mm});
            skCircle(sketch, "E8.14.0.38", {"center": v(-22.84, -29.25) * mm, "radius": 0.75 * mm});
            skCircle(sketch, "E8.14.0.39", {"center": v(-3.34, -29.25) * mm, "radius": 0.75 * mm});
            skCircle(sketch, "E8.14.0.40", {"center": v(-94.34, -29.25) * mm, "radius": 0.75 * mm});
            skCircle(sketch, "E8.14.0.41", {"center": v(-87.84, -29.25) * mm, "radius": 0.75 * mm});
            skCircle(sketch, "E8.14.0.42", {"center": v(-81.34, -29.25) * mm, "radius": 0.75 * mm});
            skCircle(sketch, "E8.14.0.43", {"center": v(-74.84, -29.25) * mm, "radius": 0.75 * mm});
            skCircle(sketch, "E8.14.0.44", {"center": v(-68.34, -29.25) * mm, "radius": 0.75 * mm});
            skCircle(sketch, "E8.14.0.45", {"center": v(-16.34, -29.25) * mm, "radius": 0.75 * mm});
            skCircle(sketch, "E8.14.0.46", {"center": v(-42.34, -29.25) * mm, "radius": 0.75 * mm});
            skCircle(sketch, "E8.14.0.47", {"center": v(-9.84, -29.25) * mm, "radius": 0.75 * mm});
            skCircle(sketch, "E8.14.0.48", {"center": v(-35.84, -29.25) * mm, "radius": 0.75 * mm});
            skCircle(sketch, "E8.14.0.49", {"center": v(-29.34, -29.25) * mm, "radius": 0.75 * mm});
            skCircle(sketch, "E8.15.0.1", {"center": v(81.2, -35.75) * mm, "radius": 0.75 * mm});
            skCircle(sketch, "E8.15.0.2", {"center": v(55.2, -35.75) * mm, "radius": 0.75 * mm});
            skCircle(sketch, "E8.15.0.3", {"center": v(22.7, -35.75) * mm, "radius": 0.75 * mm});
            skCircle(sketch, "E8.15.0.7", {"center": v(29.2, -35.75) * mm, "radius": 0.75 * mm});
            skCircle(sketch, "E8.15.0.10", {"center": v(3.2, -35.75) * mm, "radius": 0.75 * mm});
            skCircle(sketch, "E8.15.0.13", {"center": v(42.2, -35.75) * mm, "radius": 0.75 * mm});
            skCircle(sketch, "E8.15.0.14", {"center": v(87.7, -35.75) * mm, "radius": 0.75 * mm});
            skCircle(sketch, "E8.15.0.16", {"center": v(61.7, -35.75) * mm, "radius": 0.75 * mm});
            skCircle(sketch, "E8.15.0.19", {"center": v(35.7, -35.75) * mm, "radius": 0.75 * mm});
            skCircle(sketch, "E8.15.0.22", {"center": v(9.7, -35.75) * mm, "radius": 0.75 * mm});
            skCircle(sketch, "E8.15.0.24", {"center": v(94.2, -35.75) * mm, "radius": 0.75 * mm});
            skCircle(sketch, "E8.15.0.25", {"center": v(48.7, -35.75) * mm, "radius": 0.75 * mm});
            skCircle(sketch, "E8.15.0.27", {"center": v(68.2, -35.75) * mm, "radius": 0.75 * mm});
            skCircle(sketch, "E8.15.0.30", {"center": v(16.2, -35.75) * mm, "radius": 0.75 * mm});
            skCircle(sketch, "E8.15.0.32", {"center": v(74.7, -35.75) * mm, "radius": 0.75 * mm});
            skCircle(sketch, "E8.15.0.35", {"center": v(-61.8, -35.75) * mm, "radius": 0.75 * mm});
            skCircle(sketch, "E8.15.0.36", {"center": v(-55.3, -35.75) * mm, "radius": 0.75 * mm});
            skCircle(sketch, "E8.15.0.37", {"center": v(-48.8, -35.75) * mm, "radius": 0.75 * mm});
            skCircle(sketch, "E8.15.0.38", {"center": v(-22.8, -35.75) * mm, "radius": 0.75 * mm});
            skCircle(sketch, "E8.15.0.39", {"center": v(-3.3, -35.75) * mm, "radius": 0.75 * mm});
            skCircle(sketch, "E8.15.0.40", {"center": v(-94.3, -35.75) * mm, "radius": 0.75 * mm});
            skCircle(sketch, "E8.15.0.41", {"center": v(-87.8, -35.75) * mm, "radius": 0.75 * mm});
            skCircle(sketch, "E8.15.0.42", {"center": v(-81.3, -35.75) * mm, "radius": 0.75 * mm});
            skCircle(sketch, "E8.15.0.43", {"center": v(-74.8, -35.75) * mm, "radius": 0.75 * mm});
            skCircle(sketch, "E8.15.0.44", {"center": v(-68.3, -35.75) * mm, "radius": 0.75 * mm});
            skCircle(sketch, "E8.15.0.45", {"center": v(-16.3, -35.75) * mm, "radius": 0.75 * mm});
            skCircle(sketch, "E8.15.0.46", {"center": v(-42.3, -35.75) * mm, "radius": 0.75 * mm});
            skCircle(sketch, "E8.15.0.47", {"center": v(-9.8, -35.75) * mm, "radius": 0.75 * mm});
            skCircle(sketch, "E8.15.0.48", {"center": v(-35.8, -35.75) * mm, "radius": 0.75 * mm});
            skCircle(sketch, "E8.15.0.49", {"center": v(-29.3, -35.75) * mm, "radius": 0.75 * mm});
            skCircle(sketch, "E8.16.0.1", {"center": v(81.25, -42.25) * mm, "radius": 0.75 * mm});
            skCircle(sketch, "E8.16.0.2", {"center": v(55.25, -42.25) * mm, "radius": 0.75 * mm});
            skCircle(sketch, "E8.16.0.3", {"center": v(22.75, -42.25) * mm, "radius": 0.75 * mm});
            skCircle(sketch, "E8.16.0.7", {"center": v(29.25, -42.25) * mm, "radius": 0.75 * mm});
            skCircle(sketch, "E8.16.0.10", {"center": v(3.25, -42.25) * mm, "radius": 0.75 * mm});
            skCircle(sketch, "E8.16.0.13", {"center": v(42.25, -42.25) * mm, "radius": 0.75 * mm});
            skCircle(sketch, "E8.16.0.14", {"center": v(87.75, -42.25) * mm, "radius": 0.75 * mm});
            skCircle(sketch, "E8.16.0.16", {"center": v(61.75, -42.25) * mm, "radius": 0.75 * mm});
            skCircle(sketch, "E8.16.0.19", {"center": v(35.75, -42.25) * mm, "radius": 0.75 * mm});
            skCircle(sketch, "E8.16.0.22", {"center": v(9.75, -42.25) * mm, "radius": 0.75 * mm});
            skCircle(sketch, "E8.16.0.24", {"center": v(94.25, -42.25) * mm, "radius": 0.75 * mm});
            skCircle(sketch, "E8.16.0.25", {"center": v(48.75, -42.25) * mm, "radius": 0.75 * mm});
            skCircle(sketch, "E8.16.0.27", {"center": v(68.25, -42.25) * mm, "radius": 0.75 * mm});
            skCircle(sketch, "E8.16.0.30", {"center": v(16.25, -42.25) * mm, "radius": 0.75 * mm});
            skCircle(sketch, "E8.16.0.32", {"center": v(74.75, -42.25) * mm, "radius": 0.75 * mm});
            skCircle(sketch, "E8.16.0.35", {"center": v(-61.75, -42.25) * mm, "radius": 0.75 * mm});
            skCircle(sketch, "E8.16.0.36", {"center": v(-55.25, -42.25) * mm, "radius": 0.75 * mm});
            skCircle(sketch, "E8.16.0.37", {"center": v(-48.75, -42.25) * mm, "radius": 0.75 * mm});
            skCircle(sketch, "E8.16.0.38", {"center": v(-22.75, -42.25) * mm, "radius": 0.75 * mm});
            skCircle(sketch, "E8.16.0.39", {"center": v(-3.25, -42.25) * mm, "radius": 0.75 * mm});
            skCircle(sketch, "E8.16.0.40", {"center": v(-94.25, -42.25) * mm, "radius": 0.75 * mm});
            skCircle(sketch, "E8.16.0.41", {"center": v(-87.75, -42.25) * mm, "radius": 0.75 * mm});
            skCircle(sketch, "E8.16.0.42", {"center": v(-81.25, -42.25) * mm, "radius": 0.75 * mm});
            skCircle(sketch, "E8.16.0.43", {"center": v(-74.75, -42.25) * mm, "radius": 0.75 * mm});
            skCircle(sketch, "E8.16.0.44", {"center": v(-68.25, -42.25) * mm, "radius": 0.75 * mm});
            skCircle(sketch, "E8.16.0.45", {"center": v(-16.25, -42.25) * mm, "radius": 0.75 * mm});
            skCircle(sketch, "E8.16.0.46", {"center": v(-42.25, -42.25) * mm, "radius": 0.75 * mm});
            skCircle(sketch, "E8.16.0.47", {"center": v(-9.75, -42.25) * mm, "radius": 0.75 * mm});
            skCircle(sketch, "E8.16.0.48", {"center": v(-35.75, -42.25) * mm, "radius": 0.75 * mm});
            skCircle(sketch, "E8.16.0.49", {"center": v(-29.25, -42.25) * mm, "radius": 0.75 * mm});
            skCircle(sketch, "E8.17.0.1", {"center": v(81.3, -48.75) * mm, "radius": 0.75 * mm});
            skCircle(sketch, "E8.17.0.2", {"center": v(55.3, -48.75) * mm, "radius": 0.75 * mm});
            skCircle(sketch, "E8.17.0.3", {"center": v(22.8, -48.75) * mm, "radius": 0.75 * mm});
            skCircle(sketch, "E8.17.0.7", {"center": v(29.3, -48.75) * mm, "radius": 0.75 * mm});
            skCircle(sketch, "E8.17.0.10", {"center": v(3.3, -48.75) * mm, "radius": 0.75 * mm});
            skCircle(sketch, "E8.17.0.13", {"center": v(42.3, -48.75) * mm, "radius": 0.75 * mm});
            skCircle(sketch, "E8.17.0.14", {"center": v(87.8, -48.75) * mm, "radius": 0.75 * mm});
            skCircle(sketch, "E8.17.0.16", {"center": v(61.8, -48.75) * mm, "radius": 0.75 * mm});
            skCircle(sketch, "E8.17.0.19", {"center": v(35.8, -48.75) * mm, "radius": 0.75 * mm});
            skCircle(sketch, "E8.17.0.22", {"center": v(9.8, -48.75) * mm, "radius": 0.75 * mm});
            skCircle(sketch, "E8.17.0.24", {"center": v(94.3, -48.75) * mm, "radius": 0.75 * mm});
            skCircle(sketch, "E8.17.0.25", {"center": v(48.8, -48.75) * mm, "radius": 0.75 * mm});
            skCircle(sketch, "E8.17.0.27", {"center": v(68.3, -48.75) * mm, "radius": 0.75 * mm});
            skCircle(sketch, "E8.17.0.30", {"center": v(16.3, -48.75) * mm, "radius": 0.75 * mm});
            skCircle(sketch, "E8.17.0.32", {"center": v(74.8, -48.75) * mm, "radius": 0.75 * mm});
            skCircle(sketch, "E8.17.0.35", {"center": v(-61.7, -48.75) * mm, "radius": 0.75 * mm});
            skCircle(sketch, "E8.17.0.36", {"center": v(-55.2, -48.75) * mm, "radius": 0.75 * mm});
            skCircle(sketch, "E8.17.0.37", {"center": v(-48.7, -48.75) * mm, "radius": 0.75 * mm});
            skCircle(sketch, "E8.17.0.38", {"center": v(-22.7, -48.75) * mm, "radius": 0.75 * mm});
            skCircle(sketch, "E8.17.0.39", {"center": v(-3.2, -48.75) * mm, "radius": 0.75 * mm});
            skCircle(sketch, "E8.17.0.40", {"center": v(-94.2, -48.75) * mm, "radius": 0.75 * mm});
            skCircle(sketch, "E8.17.0.41", {"center": v(-87.7, -48.75) * mm, "radius": 0.75 * mm});
            skCircle(sketch, "E8.17.0.42", {"center": v(-81.2, -48.75) * mm, "radius": 0.75 * mm});
            skCircle(sketch, "E8.17.0.43", {"center": v(-74.7, -48.75) * mm, "radius": 0.75 * mm});
            skCircle(sketch, "E8.17.0.44", {"center": v(-68.2, -48.75) * mm, "radius": 0.75 * mm});
            skCircle(sketch, "E8.17.0.45", {"center": v(-16.2, -48.75) * mm, "radius": 0.75 * mm});
            skCircle(sketch, "E8.17.0.46", {"center": v(-42.2, -48.75) * mm, "radius": 0.75 * mm});
            skCircle(sketch, "E8.17.0.47", {"center": v(-9.7, -48.75) * mm, "radius": 0.75 * mm});
            skCircle(sketch, "E8.17.0.48", {"center": v(-35.7, -48.75) * mm, "radius": 0.75 * mm});
            skCircle(sketch, "E8.17.0.49", {"center": v(-29.2, -48.75) * mm, "radius": 0.75 * mm});
            skCircle(sketch, "E8.18.0.1", {"center": v(81.34, -55.25) * mm, "radius": 0.75 * mm});
            skCircle(sketch, "E8.18.0.2", {"center": v(55.34, -55.25) * mm, "radius": 0.75 * mm});
            skCircle(sketch, "E8.18.0.3", {"center": v(22.84, -55.25) * mm, "radius": 0.75 * mm});
            skCircle(sketch, "E8.18.0.7", {"center": v(29.34, -55.25) * mm, "radius": 0.75 * mm});
            skCircle(sketch, "E8.18.0.10", {"center": v(3.34, -55.25) * mm, "radius": 0.75 * mm});
            skCircle(sketch, "E8.18.0.13", {"center": v(42.34, -55.25) * mm, "radius": 0.75 * mm});
            skCircle(sketch, "E8.18.0.14", {"center": v(87.84, -55.25) * mm, "radius": 0.75 * mm});
            skCircle(sketch, "E8.18.0.16", {"center": v(61.84, -55.25) * mm, "radius": 0.75 * mm});
            skCircle(sketch, "E8.18.0.19", {"center": v(35.84, -55.25) * mm, "radius": 0.75 * mm});
            skCircle(sketch, "E8.18.0.22", {"center": v(9.84, -55.25) * mm, "radius": 0.75 * mm});
            skCircle(sketch, "E8.18.0.24", {"center": v(94.34, -55.25) * mm, "radius": 0.75 * mm});
            skCircle(sketch, "E8.18.0.25", {"center": v(48.84, -55.25) * mm, "radius": 0.75 * mm});
            skCircle(sketch, "E8.18.0.27", {"center": v(68.34, -55.25) * mm, "radius": 0.75 * mm});
            skCircle(sketch, "E8.18.0.30", {"center": v(16.34, -55.25) * mm, "radius": 0.75 * mm});
            skCircle(sketch, "E8.18.0.32", {"center": v(74.84, -55.25) * mm, "radius": 0.75 * mm});
            skCircle(sketch, "E8.18.0.35", {"center": v(-61.66, -55.25) * mm, "radius": 0.75 * mm});
            skCircle(sketch, "E8.18.0.36", {"center": v(-55.16, -55.25) * mm, "radius": 0.75 * mm});
            skCircle(sketch, "E8.18.0.37", {"center": v(-48.66, -55.25) * mm, "radius": 0.75 * mm});
            skCircle(sketch, "E8.18.0.38", {"center": v(-22.66, -55.25) * mm, "radius": 0.75 * mm});
            skCircle(sketch, "E8.18.0.39", {"center": v(-3.16, -55.25) * mm, "radius": 0.75 * mm});
            skCircle(sketch, "E8.18.0.40", {"center": v(-94.16, -55.25) * mm, "radius": 0.75 * mm});
            skCircle(sketch, "E8.18.0.41", {"center": v(-87.66, -55.25) * mm, "radius": 0.75 * mm});
            skCircle(sketch, "E8.18.0.42", {"center": v(-81.16, -55.25) * mm, "radius": 0.75 * mm});
            skCircle(sketch, "E8.18.0.43", {"center": v(-74.66, -55.25) * mm, "radius": 0.75 * mm});
            skCircle(sketch, "E8.18.0.44", {"center": v(-68.16, -55.25) * mm, "radius": 0.75 * mm});
            skCircle(sketch, "E8.18.0.45", {"center": v(-16.16, -55.25) * mm, "radius": 0.75 * mm});
            skCircle(sketch, "E8.18.0.46", {"center": v(-42.16, -55.25) * mm, "radius": 0.75 * mm});
            skCircle(sketch, "E8.18.0.47", {"center": v(-9.66, -55.25) * mm, "radius": 0.75 * mm});
            skCircle(sketch, "E8.18.0.48", {"center": v(-35.66, -55.25) * mm, "radius": 0.75 * mm});
            skCircle(sketch, "E8.18.0.49", {"center": v(-29.16, -55.25) * mm, "radius": 0.75 * mm});
            skCircle(sketch, "E8.19.0.1", {"center": v(81.4, -61.75) * mm, "radius": 0.75 * mm});
            skCircle(sketch, "E8.19.0.2", {"center": v(55.4, -61.75) * mm, "radius": 0.75 * mm});
            skCircle(sketch, "E8.19.0.3", {"center": v(22.9, -61.75) * mm, "radius": 0.75 * mm});
            skCircle(sketch, "E8.19.0.7", {"center": v(29.4, -61.75) * mm, "radius": 0.75 * mm});
            skCircle(sketch, "E8.19.0.10", {"center": v(3.4, -61.75) * mm, "radius": 0.75 * mm});
            skCircle(sketch, "E8.19.0.13", {"center": v(42.4, -61.75) * mm, "radius": 0.75 * mm});
            skCircle(sketch, "E8.19.0.14", {"center": v(87.9, -61.75) * mm, "radius": 0.75 * mm});
            skCircle(sketch, "E8.19.0.16", {"center": v(61.9, -61.75) * mm, "radius": 0.75 * mm});
            skCircle(sketch, "E8.19.0.19", {"center": v(35.9, -61.75) * mm, "radius": 0.75 * mm});
            skCircle(sketch, "E8.19.0.22", {"center": v(9.9, -61.75) * mm, "radius": 0.75 * mm});
            skCircle(sketch, "E8.19.0.24", {"center": v(94.4, -61.75) * mm, "radius": 0.75 * mm});
            skCircle(sketch, "E8.19.0.25", {"center": v(48.9, -61.75) * mm, "radius": 0.75 * mm});
            skCircle(sketch, "E8.19.0.27", {"center": v(68.4, -61.75) * mm, "radius": 0.75 * mm});
            skCircle(sketch, "E8.19.0.30", {"center": v(16.4, -61.75) * mm, "radius": 0.75 * mm});
            skCircle(sketch, "E8.19.0.32", {"center": v(74.9, -61.75) * mm, "radius": 0.75 * mm});
            skCircle(sketch, "E8.19.0.35", {"center": v(-61.6, -61.75) * mm, "radius": 0.75 * mm});
            skCircle(sketch, "E8.19.0.36", {"center": v(-55.1, -61.75) * mm, "radius": 0.75 * mm});
            skCircle(sketch, "E8.19.0.37", {"center": v(-48.6, -61.75) * mm, "radius": 0.75 * mm});
            skCircle(sketch, "E8.19.0.38", {"center": v(-22.6, -61.75) * mm, "radius": 0.75 * mm});
            skCircle(sketch, "E8.19.0.39", {"center": v(-3.1, -61.75) * mm, "radius": 0.75 * mm});
            skCircle(sketch, "E8.19.0.40", {"center": v(-94.1, -61.75) * mm, "radius": 0.75 * mm});
            skCircle(sketch, "E8.19.0.41", {"center": v(-87.6, -61.75) * mm, "radius": 0.75 * mm});
            skCircle(sketch, "E8.19.0.42", {"center": v(-81.1, -61.75) * mm, "radius": 0.75 * mm});
            skCircle(sketch, "E8.19.0.43", {"center": v(-74.6, -61.75) * mm, "radius": 0.75 * mm});
            skCircle(sketch, "E8.19.0.44", {"center": v(-68.1, -61.75) * mm, "radius": 0.75 * mm});
            skCircle(sketch, "E8.19.0.45", {"center": v(-16.1, -61.75) * mm, "radius": 0.75 * mm});
            skCircle(sketch, "E8.19.0.46", {"center": v(-42.1, -61.75) * mm, "radius": 0.75 * mm});
            skCircle(sketch, "E8.19.0.47", {"center": v(-9.6, -61.75) * mm, "radius": 0.75 * mm});
            skCircle(sketch, "E8.19.0.48", {"center": v(-35.6, -61.75) * mm, "radius": 0.75 * mm});
            skCircle(sketch, "E8.19.0.49", {"center": v(-29.1, -61.75) * mm, "radius": 0.75 * mm});
            skLineSegment(sketch, "E8.direction1", {"start": v(-95, 61.75) * mm, "end": v(-94.95, 55.25) * mm, "construction": true});
            skLineSegment(sketch, "E9", {"start": v(100, -67.5) * mm, "end": v(100, 67.5) * mm});
            skSolve(sketch);
        }
        {
            var Q0;
            Q0=makeQuery(id+"F0.imprint","IMPRINT",FACE,{"disambiguationData":[TD([[makeQuery(id+"F0.imprint","IMPRINT",EDGE,{"derivedFrom":sQuery(id+"F0.wireOp",EDGE,"E0.bottom")}),1.0]])]});
            extrude(context, id + "F1", {"entities" : qUnion([Q0]), "depth" : 1.5 * mm});
        }
    });
